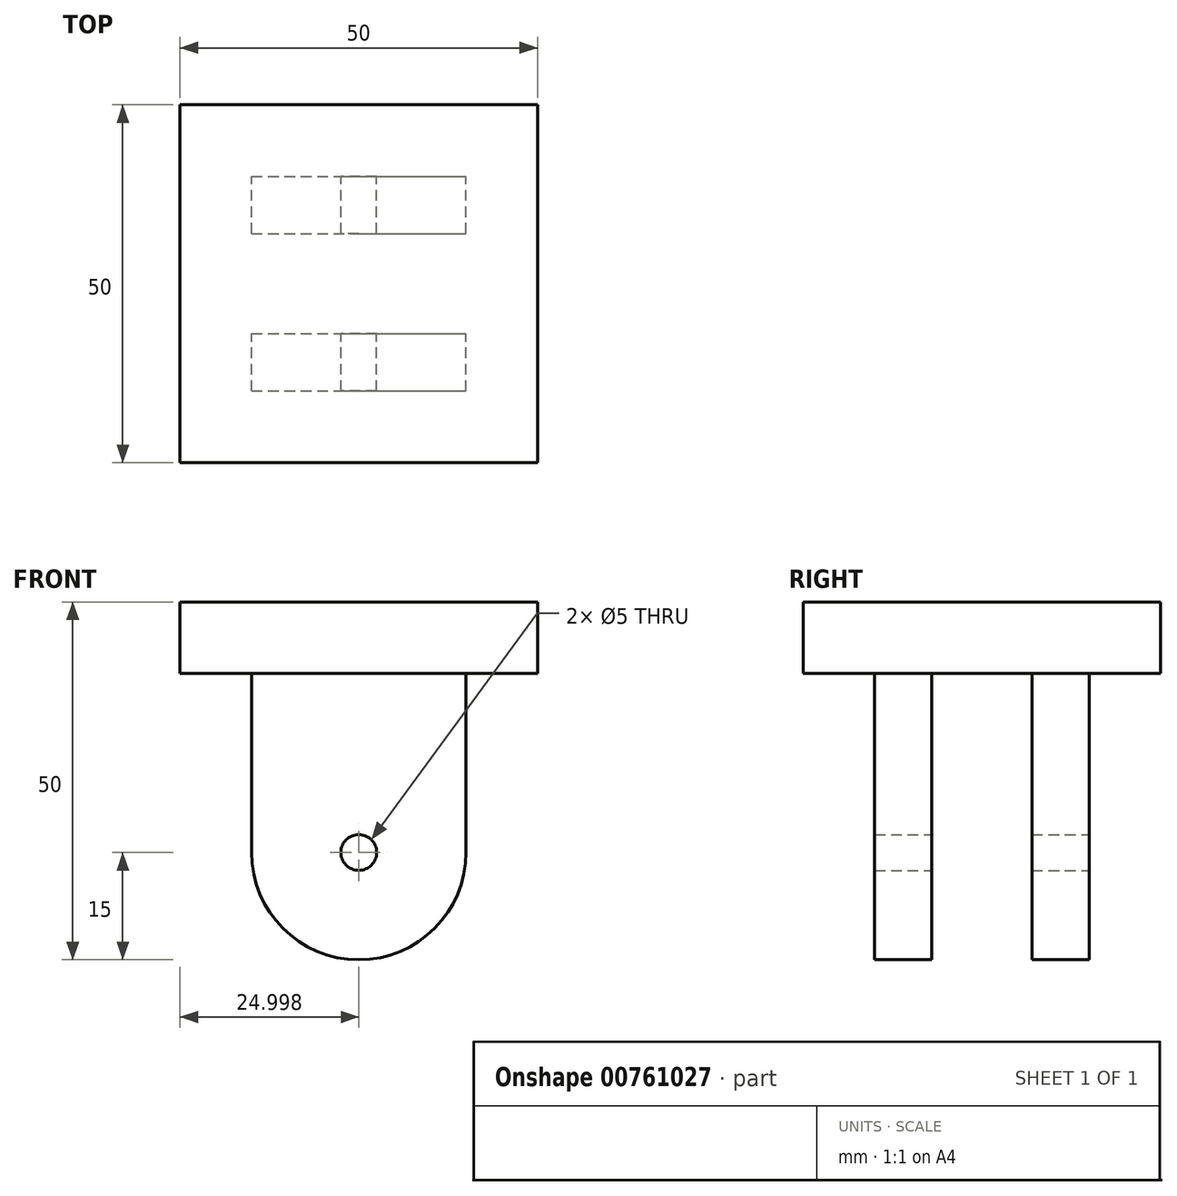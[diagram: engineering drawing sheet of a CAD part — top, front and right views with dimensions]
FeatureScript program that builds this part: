
annotation { "Feature Type Name" : "Feature", "Feature Type Description" : "" }
export const myFeature = defineFeature(function(context is Context, id is Id, definition is map)
    precondition{}
    {
        {
            var Q0;
            Q0=qCreatedBy(makeId("Top.planeOp"),FACE);
            var sketch = newSketch(context, id + "F0", { "sketchPlane" : qUnion([Q0])});
            skLineSegment(sketch, "E0.bottom", {"start": v(-22.53, 23.2) * mm, "end": v(27.47, 23.2) * mm});
            skLineSegment(sketch, "E0.top", {"start": v(-22.53, -26.8) * mm, "end": v(27.47, -26.8) * mm});
            skLineSegment(sketch, "E0.left", {"start": v(-22.53, 23.2) * mm, "end": v(-22.53, -26.8) * mm});
            skLineSegment(sketch, "E0.right", {"start": v(27.47, 23.2) * mm, "end": v(27.47, -26.8) * mm});
            skSolve(sketch);
        }
        {
            var Q0;
            Q0=makeQuery(id+"F0.imprint","IMPRINT",FACE,{"disambiguationData":[TD([[makeQuery(id+"F0.imprint","IMPRINT",EDGE,{"derivedFrom":sQuery(id+"F0.wireOp",EDGE,"E0.bottom")}),-1.0]])]});
            extrude(context, id + "F1", {"entities" : qUnion([Q0]), "depth" : 10 * mm, "offsetDistance" : 25 * mm});
        }
        {
            var Q0;
            Q0=makeQuery(id+"F1.opExtrude","CAP_FACE",FACE,{"disambiguationData":[OSD([sQuery(id+"F0.wireOp",EDGE,"E0.bottom"),sQuery(id+"F0.wireOp",EDGE,"E0.top"),sQuery(id+"F0.wireOp",EDGE,"E0.left"),sQuery(id+"F0.wireOp",EDGE,"E0.right")])],"isStart":true});
            var sketch = newSketch(context, id + "F2", { "sketchPlane" : qUnion([Q0])});
            skLineSegment(sketch, "E1.bottom", {"start": v(-12.53, 16.8) * mm, "end": v(17.47, 16.8) * mm});
            skLineSegment(sketch, "E1.top", {"start": v(-12.53, 8.8) * mm, "end": v(17.47, 8.8) * mm});
            skLineSegment(sketch, "E1.left", {"start": v(-12.53, 16.8) * mm, "end": v(-12.53, 8.8) * mm});
            skLineSegment(sketch, "E1.right", {"start": v(17.47, 16.8) * mm, "end": v(17.47, 8.8) * mm});
            skLineSegment(sketch, "E2", {"start": v(2.47, 16.8) * mm, "end": v(2.47, 26.8) * mm});
            skLineSegment(sketch, "E3", {"start": v(17.47, 12.8) * mm, "end": v(27.47, 12.8) * mm});
            skLineSegment(sketch, "E4.bottom", {"start": v(-12.53, -5.2) * mm, "end": v(17.47, -5.2) * mm});
            skLineSegment(sketch, "E4.top", {"start": v(-12.53, -13.2) * mm, "end": v(17.47, -13.2) * mm});
            skLineSegment(sketch, "E4.left", {"start": v(-12.53, -5.2) * mm, "end": v(-12.53, -13.2) * mm});
            skLineSegment(sketch, "E4.right", {"start": v(17.47, -5.2) * mm, "end": v(17.47, -13.2) * mm});
            skLineSegment(sketch, "E5", {"start": v(2.47, -23.2) * mm, "end": v(2.47, -13.2) * mm});
            skLineSegment(sketch, "E6", {"start": v(-12.53, -9.2) * mm, "end": v(-22.53, -9.2) * mm});
            skSolve(sketch);
        }
        {
            var Q0;
            {var subQ1=sQuery(id+"F2.wireOp",EDGE,"E1.top");Q0=makeQuery(id+"F2.imprint","IMPRINT",FACE,{"disambiguationData":[TD([[makeQuery(id+"F2.imprint","IMPRINT",EDGE,{"derivedFrom":subQ1}),1.0]])]});}
            var Q1;
            {var subQ1=sQuery(id+"F2.wireOp",EDGE,"E4.bottom");Q1=makeQuery(id+"F2.imprint","IMPRINT",FACE,{"disambiguationData":[TD([[makeQuery(id+"F2.imprint","IMPRINT",EDGE,{"derivedFrom":subQ1}),-1.0]])]});}
            extrude(context, id + "F3", {"entities" : qUnion([Q0, Q1]), "operationType" : NewBodyOperationType.ADD, "depth" : 40 * mm, "offsetDistance" : 25 * mm});
        }
        {
            var Q0;
            Q0=makeQuery(id+"F3.opExtrude","CAP_EDGE",EDGE,{"disambiguationData":[OSD([sQuery(id+"F2.wireOp",EDGE,"E4.right")])],"isStart":false});
            fillet(context, id + "F4", {"entities" : qUnion([Q0]), "radius" : 15 * mm, "tangentPropagation" : true, "allowEdgeOverflow" : false});
        }
        {
            var Q0;
            Q0=makeQuery(id+"F3.opExtrude","CAP_EDGE",EDGE,{"disambiguationData":[OSD([sQuery(id+"F2.wireOp",EDGE,"E1.right")])],"isStart":false});
            fillet(context, id + "F5", {"entities" : qUnion([Q0]), "radius" : 15 * mm, "tangentPropagation" : true, "allowEdgeOverflow" : false});
        }
        {
            var Q0;
            Q0=makeQuery(id+"F3.opExtrude","CAP_EDGE",EDGE,{"disambiguationData":[OSD([sQuery(id+"F2.wireOp",EDGE,"E4.left")])],"isStart":false});
            fillet(context, id + "F6", {"entities" : qUnion([Q0]), "radius" : 15 * mm, "tangentPropagation" : true, "allowEdgeOverflow" : false});
        }
        {
            var Q0;
            Q0=makeQuery(id+"F3.opExtrude","CAP_EDGE",EDGE,{"disambiguationData":[OSD([sQuery(id+"F2.wireOp",EDGE,"E1.left")])],"isStart":false});
            fillet(context, id + "F7", {"entities" : qUnion([Q0]), "radius" : 15 * mm, "tangentPropagation" : true, "allowEdgeOverflow" : false});
        }
        {
            var Q0;
            Q0=makeQuery(id+"F3.opExtrude","SWEPT_FACE",FACE,{"disambiguationData":[OSD([sQuery(id+"F2.wireOp",EDGE,"E4.top")])]});
            var sketch = newSketch(context, id + "F8", { "sketchPlane" : qUnion([Q0])});
            skCircle(sketch, "E7", {"center": v(-2.47, -25) * mm, "radius": 2.5 * mm});
            skSolve(sketch);
        }
        {
            var Q0;
            Q0=sQuery(id+"F8.wireOp",VERTEX,"E7.center");
            var Q1;
            Q1=makeQuery(id+"F1.opExtrude","SWEPT_BODY",BODY,{"disambiguationData":[OSD([sQuery(id+"F0.wireOp",EDGE,"E0.bottom"),sQuery(id+"F0.wireOp",EDGE,"E0.top"),sQuery(id+"F0.wireOp",EDGE,"E0.left"),sQuery(id+"F0.wireOp",EDGE,"E0.right")])]});
            hole(context, id + "F9", {"style" : HoleStyle.SIMPLE, "endStyle" : HoleEndStyle.THROUGH, "holeDiameter" : 5 * mm, "majorDiameter" : 5 * mm, "isTappedThrough" : true, "tappedDepth" : 12 * mm, "tapClearance" : 3, "locations" : qUnion([Q0]), "scope" : qUnion([Q1])});
        }
    });
